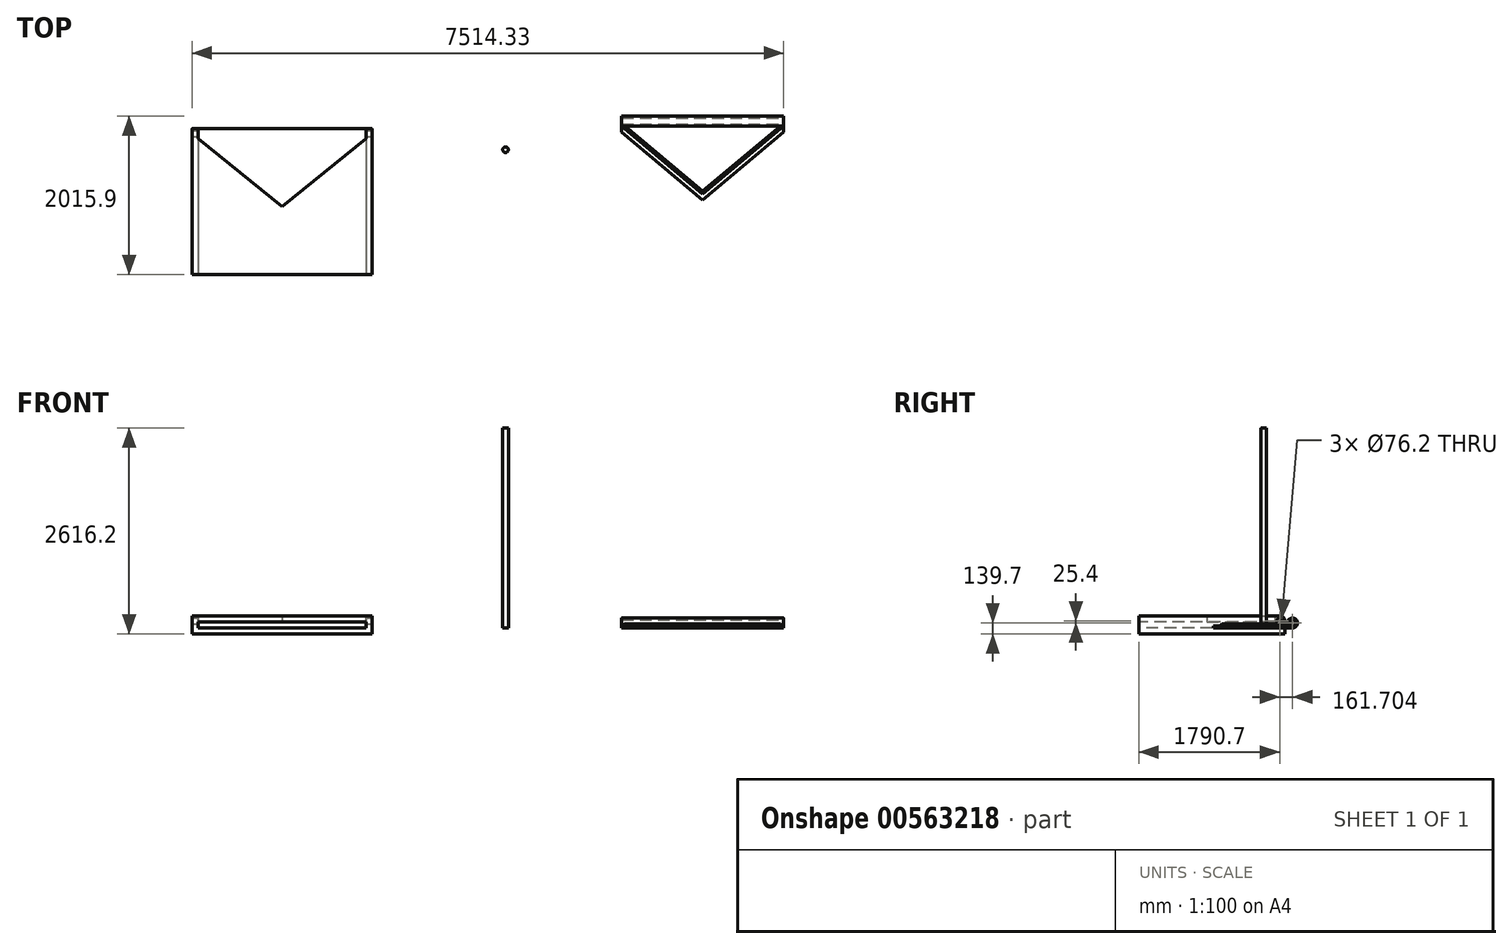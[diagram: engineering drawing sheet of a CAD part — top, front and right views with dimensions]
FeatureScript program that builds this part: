
annotation { "Feature Type Name" : "Feature", "Feature Type Description" : "" }
export const myFeature = defineFeature(function(context is Context, id is Id, definition is map)
    precondition{}
    {
        {
            var Q0;
            Q0=qCreatedBy(makeId("Top.planeOp"),FACE);
            var sketch = newSketch(context, id + "F0", { "sketchPlane" : qUnion([Q0])});
            skLineSegment(sketch, "E0.bottom", {"start": v(-1143, 863.6) * mm, "end": v(1143, 863.6) * mm});
            skLineSegment(sketch, "E0.top", {"start": v(-1143, -863.6) * mm, "end": v(1143, -863.6) * mm});
            skLineSegment(sketch, "E0.left", {"start": v(-1143, 863.6) * mm, "end": v(-1143, -863.6) * mm});
            skLineSegment(sketch, "E0.right", {"start": v(1143, 863.6) * mm, "end": v(1143, -863.6) * mm});
            skPoint(sketch, "E0.middle", {"position": v(0, 0) * mm});
            skSolve(sketch);
        }
        {
            var Q0;
            Q0 = qSketchRegion(id + "F0", true);
            extrude(context, id + "F1", {"entities" : qUnion([Q0]), "depth" : 76.2 * mm, "offsetDistance" : 25.4 * mm});
        }
        {
            var Q0;
            Q0=makeQuery(id+"F1.opExtrude","CAP_FACE",FACE,{"disambiguationData":[OSD([sQuery(id+"F0.wireOp",EDGE,"E0.bottom"),sQuery(id+"F0.wireOp",EDGE,"E0.top"),sQuery(id+"F0.wireOp",EDGE,"E0.left"),sQuery(id+"F0.wireOp",EDGE,"E0.right")])],"isStart":false});
            var sketch = newSketch(context, id + "F2", { "sketchPlane" : qUnion([Q0])});
            skLineSegment(sketch, "E1.bottom", {"start": v(-1143, 863.6) * mm, "end": v(-1066.8, 863.6) * mm});
            skLineSegment(sketch, "E1.top", {"start": v(-1143, -863.6) * mm, "end": v(-1066.8, -863.6) * mm});
            skLineSegment(sketch, "E1.left", {"start": v(-1143, 863.6) * mm, "end": v(-1143, -863.6) * mm});
            skLineSegment(sketch, "E1.right", {"start": v(-1066.8, 863.6) * mm, "end": v(-1066.8, -863.6) * mm});
            skLineSegment(sketch, "E2.bottom", {"start": v(1143, 863.6) * mm, "end": v(1066.8, 863.6) * mm});
            skLineSegment(sketch, "E2.top", {"start": v(1143, -863.6) * mm, "end": v(1066.8, -863.6) * mm});
            skLineSegment(sketch, "E2.left", {"start": v(1143, 863.6) * mm, "end": v(1143, -863.6) * mm});
            skLineSegment(sketch, "E2.right", {"start": v(1066.8, 863.6) * mm, "end": v(1066.8, -863.6) * mm});
            skSolve(sketch);
        }
        {
            var Q0;
            Q0 = qSketchRegion(id + "F2", true);
            extrude(context, id + "F3", {"entities" : qUnion([Q0]), "operationType" : NewBodyOperationType.ADD, "depth" : 76.2 * mm, "offsetDistance" : 25.4 * mm});
        }
        {
            var Q0;
            Q0=makeQuery(id+"F1.opExtrude","CAP_FACE",FACE,{"disambiguationData":[OSD([sQuery(id+"F0.wireOp",EDGE,"E0.bottom"),sQuery(id+"F0.wireOp",EDGE,"E0.top"),sQuery(id+"F0.wireOp",EDGE,"E0.left"),sQuery(id+"F0.wireOp",EDGE,"E0.right")])],"isStart":false});
            var sketch = newSketch(context, id + "F4", { "sketchPlane" : qUnion([Q0])});
            skLineSegment(sketch, "E3.bottom", {"start": v(-1143, -863.6) * mm, "end": v(1143, -863.6) * mm});
            skLineSegment(sketch, "E3.top", {"start": v(-1143, 863.6) * mm, "end": v(1143, 863.6) * mm});
            skLineSegment(sketch, "E3.left", {"start": v(-1143, -863.6) * mm, "end": v(-1143, 863.6) * mm});
            skLineSegment(sketch, "E3.right", {"start": v(1143, -863.6) * mm, "end": v(1143, 863.6) * mm});
            skPoint(sketch, "E3.middle", {"position": v(0, 0) * mm});
            skLineSegment(sketch, "E4", {"start": v(0, 0) * mm, "end": v(-1066.8, 863.6) * mm});
            skLineSegment(sketch, "E5", {"start": v(0, 0) * mm, "end": v(1066.8, 863.6) * mm});
            skSolve(sketch);
        }
        {
            var Q0;
            {var subQ2=sQuery(id+"F4.wireOp",EDGE,"E3.left");Q0=makeQuery(id+"F4.imprint","IMPRINT",FACE,{"disambiguationData":[TD([[makeQuery(id+"F4.imprint","IMPRINT",EDGE,{"derivedFrom":subQ2}),-1.0]])]});}
            var Q1;
            {var subQ2=sQuery(id+"F4.wireOp",EDGE,"E3.right");Q1=makeQuery(id+"F4.imprint","IMPRINT",FACE,{"disambiguationData":[TD([[makeQuery(id+"F4.imprint","IMPRINT",EDGE,{"derivedFrom":subQ2}),1.0]])]});}
            var Q2;
            Q2=makeQuery(id+"F4.imprint","IMPRINT",FACE,{"disambiguationData":[TD([[makeQuery(id+"F4.imprint","IMPRINT",EDGE,{"derivedFrom":sQuery(id+"F4.wireOp",EDGE,"E4")}),1.0]])]});
            extrude(context, id + "F5", {"entities" : qUnion([Q0, Q1, Q2]), "operationType" : NewBodyOperationType.ADD, "depth" : 152.4 * mm, "offsetDistance" : 25.4 * mm, "hasSecondDirection" : true, "secondDirectionOppositeDirection" : false, "secondDirectionDepth" : 76.2 * mm});
        }
        {
            var Q0;
            {var subQ0=sQuery(id+"F4.wireOp",EDGE,"E3.top");Q0=makeQuery(id+"F5.boolean.opBoolean","MERGE",FACE,{"derivedFrom":[makeQuery(id+"F3.boolean.opBoolean","MERGE",FACE,{"derivedFrom":[makeQuery(id+"F1.opExtrude","SWEPT_FACE",FACE,{"disambiguationData":[OSD([sQuery(id+"F0.wireOp",EDGE,"E0.bottom")])]}),makeQuery(id+"F3.opExtrude","SWEPT_FACE",FACE,{"disambiguationData":[OSD([sQuery(id+"F2.wireOp",EDGE,"E1.bottom")])]}),makeQuery(id+"F3.opExtrude","SWEPT_FACE",FACE,{"disambiguationData":[OSD([sQuery(id+"F2.wireOp",EDGE,"E2.bottom")])]})]}),makeQuery(id+"F5.opExtrude","SWEPT_FACE",FACE,{"disambiguationData":[OSD([subQ0]),TDD([makeQuery(id+"F4.imprint","IMPRINT",EDGE,{"disambiguationData":[TD([[makeQuery(id+"F4.imprint","INTERSECT",VERTEX,{"derivedFrom":[subQ0,sQuery(id+"F4.wireOp",EDGE,"E3.left")]}),-1.0]])],"derivedFrom":subQ0})])]}),makeQuery(id+"F5.opExtrude","SWEPT_FACE",FACE,{"disambiguationData":[OSD([subQ0]),TDD([makeQuery(id+"F4.imprint","IMPRINT",EDGE,{"disambiguationData":[TD([[makeQuery(id+"F4.imprint","INTERSECT",VERTEX,{"derivedFrom":[subQ0,sQuery(id+"F4.wireOp",EDGE,"E3.right")]}),1.0]])],"derivedFrom":subQ0})])]})]});}
            var sketch = newSketch(context, id + "F6", { "sketchPlane" : qUnion([Q0])});
            skLineSegment(sketch, "E6.bottom", {"start": v(-1143, 0) * mm, "end": v(-1066.8, 0) * mm});
            skLineSegment(sketch, "E6.top", {"start": v(-1143, 228.6) * mm, "end": v(-1066.8, 228.6) * mm});
            skLineSegment(sketch, "E6.left", {"start": v(-1143, 0) * mm, "end": v(-1143, 228.6) * mm});
            skLineSegment(sketch, "E6.right", {"start": v(-1066.8, 0) * mm, "end": v(-1066.8, 228.6) * mm});
            skLineSegment(sketch, "E7.bottom", {"start": v(1143, 0) * mm, "end": v(1066.8, 0) * mm});
            skLineSegment(sketch, "E7.top", {"start": v(1143, 228.6) * mm, "end": v(1066.8, 228.6) * mm});
            skLineSegment(sketch, "E7.left", {"start": v(1143, 0) * mm, "end": v(1143, 228.6) * mm});
            skLineSegment(sketch, "E7.right", {"start": v(1066.8, 0) * mm, "end": v(1066.8, 228.6) * mm});
            skSolve(sketch);
        }
        {
            var Q0;
            {var subQ3=sQuery(id+"F6.wireOp",EDGE,"E6.bottom");Q0=makeQuery(id+"F6.imprint","IMPRINT",FACE,{"disambiguationData":[TD([[makeQuery(id+"F6.imprint","IMPRINT",EDGE,{"derivedFrom":subQ3}),-1.0]])]});}
            var Q1;
            {var subQ3=sQuery(id+"F6.wireOp",EDGE,"E7.bottom");Q1=makeQuery(id+"F6.imprint","IMPRINT",FACE,{"disambiguationData":[TD([[makeQuery(id+"F6.imprint","IMPRINT",EDGE,{"derivedFrom":subQ3}),-1.0]])]});}
            var Q2;
            {var subQ1=sQuery(id+"F0.wireOp",EDGE,"E0.bottom");var subQ2=makeQuery(id+"F1.opExtrude","CAP_EDGE",EDGE,{"disambiguationData":[OSD([subQ1])],"isStart":false});Q2=makeQuery(id+"F6.imprint","IMPRINT",FACE,{"disambiguationData":[TD([[makeQuery(id+"F6.imprint","IMPRINT",EDGE,{"derivedFrom":subQ2}),1.0]])]});}
            extrude(context, id + "F7", {"entities" : qUnion([Q0, Q1, Q2]), "operationType" : NewBodyOperationType.ADD, "depth" : 127 * mm, "offsetDistance" : 25.4 * mm});
        }
        {
            var Q0;
            {var subQ0=sQuery(id+"F0.wireOp",EDGE,"E0.bottom");Q0=makeQuery(id+"F7.boolean.opBoolean","MERGE",FACE,{"derivedFrom":[makeQuery(id+"F1.opExtrude","CAP_FACE",FACE,{"disambiguationData":[OSD([subQ0,sQuery(id+"F0.wireOp",EDGE,"E0.top"),sQuery(id+"F0.wireOp",EDGE,"E0.left"),sQuery(id+"F0.wireOp",EDGE,"E0.right")])],"isStart":false}),makeQuery(id+"F7.opExtrude","SWEPT_FACE",FACE,{"disambiguationData":[OSD([subQ0])]})]});}
            var sketch = newSketch(context, id + "F8", { "sketchPlane" : qUnion([Q0])});
            skSolve(sketch);
        }
        {
            var Q0;
            Q0=makeQuery(id+"F7.boolean.opBoolean","MERGE",FACE,{"derivedFrom":[makeQuery(id+"F5.boolean.opBoolean","MERGE",FACE,{"derivedFrom":[makeQuery(id+"F3.boolean.opBoolean","MERGE",FACE,{"derivedFrom":[makeQuery(id+"F1.opExtrude","SWEPT_FACE",FACE,{"disambiguationData":[OSD([sQuery(id+"F0.wireOp",EDGE,"E0.right")])]}),makeQuery(id+"F3.opExtrude","SWEPT_FACE",FACE,{"disambiguationData":[OSD([sQuery(id+"F2.wireOp",EDGE,"E2.left")])]})]}),makeQuery(id+"F5.opExtrude","SWEPT_FACE",FACE,{"disambiguationData":[OSD([sQuery(id+"F4.wireOp",EDGE,"E3.right")])]})]}),makeQuery(id+"F7.opExtrude","SWEPT_FACE",FACE,{"disambiguationData":[OSD([sQuery(id+"F6.wireOp",EDGE,"E6.left")])]})]});
            var sketch = newSketch(context, id + "F9", { "sketchPlane" : qUnion([Q0])});
            skCircle(sketch, "E8", {"center": v(927.1, 165.1) * mm, "radius": 38.1 * mm});
            skSolve(sketch);
        }
        {
            var Q0;
            Q0=makeQuery(id+"F9.imprint","IMPRINT",FACE,{"disambiguationData":[TD([[makeQuery(id+"F9.imprint","IMPRINT",EDGE,{"derivedFrom":sQuery(id+"F9.wireOp",EDGE,"E8")}),1.0]])]});
            extrude(context, id + "F10", {"entities" : qUnion([Q0]), "operationType" : NewBodyOperationType.REMOVE, "oppositeDirection" : true, "depth" : 2291.08 * mm, "offsetDistance" : 25.4 * mm});
        }
        {
            var Q0;
            Q0=makeQuery(id+"F8.imprint","IMPRINT",FACE,{"disambiguationData":[TD([[makeQuery(id+"F8.imprint","IMPRINT",EDGE,{"derivedFrom":makeQuery(id+"F1.opExtrude","CAP_EDGE",EDGE,{"disambiguationData":[OSD([sQuery(id+"F0.wireOp",EDGE,"E0.top")])],"isStart":false})}),1.0]])]});
            var sketch = newSketch(context, id + "F11", { "sketchPlane" : qUnion([Q0])});
            skLineSegment(sketch, "E9.bottom", {"start": v(4313.93, 1025.3) * mm, "end": v(6371.33, 1025.3) * mm});
            skLineSegment(sketch, "E9.top", {"start": v(4313.93, 161.7) * mm, "end": v(6371.33, 161.7) * mm});
            skLineSegment(sketch, "E9.left", {"start": v(4313.93, 1025.3) * mm, "end": v(4313.93, 161.7) * mm});
            skLineSegment(sketch, "E9.right", {"start": v(6371.33, 1025.3) * mm, "end": v(6371.33, 161.7) * mm});
            skPoint(sketch, "E10", {"position": v(5342.63, 161.7) * mm});
            skLineSegment(sketch, "E11", {"start": v(4313.93, 1025.3) * mm, "end": v(5342.63, 161.7) * mm});
            skLineSegment(sketch, "E12", {"start": v(6371.33, 1025.3) * mm, "end": v(5342.63, 161.7) * mm});
            skLineSegment(sketch, "E13", {"start": v(5342.63, 161.7) * mm, "end": v(5342.63, 9.3) * mm});
            skPoint(sketch, "E14", {"position": v(4313.93, 949.1) * mm});
            skPoint(sketch, "E15", {"position": v(6371.33, 949.1) * mm});
            skPoint(sketch, "E16", {"position": v(5342.63, 85.5) * mm});
            skLineSegment(sketch, "E17", {"start": v(4313.93, 949.1) * mm, "end": v(5342.63, 85.5) * mm});
            skLineSegment(sketch, "E18", {"start": v(6371.33, 949.1) * mm, "end": v(5342.63, 85.5) * mm});
            skLineSegment(sketch, "E19.top", {"start": v(4313.93, 1152.3) * mm, "end": v(6371.33, 1152.3) * mm});
            skLineSegment(sketch, "E19.left", {"start": v(4313.93, 1025.3) * mm, "end": v(4313.93, 1152.3) * mm});
            skLineSegment(sketch, "E19.right", {"start": v(6371.33, 1025.3) * mm, "end": v(6371.33, 1152.3) * mm});
            skSolve(sketch);
        }
        {
            var Q0;
            Q0=makeQuery(id+"F11.imprint","IMPRINT",FACE,{"disambiguationData":[TD([[makeQuery(id+"F11.imprint","IMPRINT",EDGE,{"derivedFrom":sQuery(id+"F11.wireOp",EDGE,"E9.bottom")}),-1.0]])]});
            var Q1;
            Q1=makeQuery(id+"F11.imprint","IMPRINT",FACE,{"disambiguationData":[TD([[makeQuery(id+"F11.imprint","IMPRINT",EDGE,{"derivedFrom":sQuery(id+"F11.wireOp",EDGE,"E11")}),1.0]])]});
            extrude(context, id + "F12", {"entities" : qUnion([Q0, Q1]), "depth" : 50.8 * mm, "offsetDistance" : 25.4 * mm});
        }
        {
            var Q0;
            {var subQ0=sQuery(id+"F11.wireOp",EDGE,"E11");Q0=makeQuery(id+"F11.imprint","IMPRINT",FACE,{"disambiguationData":[TD([[makeQuery(id+"F11.imprint","IMPRINT",EDGE,{"derivedFrom":subQ0}),-1.0]])]});}
            var Q1;
            {var subQ0=sQuery(id+"F11.wireOp",EDGE,"E12");Q1=makeQuery(id+"F11.imprint","IMPRINT",FACE,{"disambiguationData":[TD([[makeQuery(id+"F11.imprint","IMPRINT",EDGE,{"derivedFrom":subQ0}),1.0]])]});}
            var Q2;
            {var subQ1=sQuery(id+"F11.wireOp",EDGE,"E9.top");var subQ3=sQuery(id+"F11.wireOp",EDGE,"E18");var subQ4=makeQuery(id+"F11.imprint","INTERSECT",VERTEX,{"derivedFrom":[subQ1,subQ3]});Q2=makeQuery(id+"F11.imprint","IMPRINT",FACE,{"disambiguationData":[TD([[makeQuery(id+"F11.imprint","IMPRINT",EDGE,{"disambiguationData":[TD([[subQ4,-1.0]])],"derivedFrom":subQ3}),-1.0]])]});}
            var Q3;
            {var subQ1=sQuery(id+"F11.wireOp",EDGE,"E9.top");var subQ3=sQuery(id+"F11.wireOp",EDGE,"E17");var subQ4=makeQuery(id+"F11.imprint","INTERSECT",VERTEX,{"derivedFrom":[subQ1,subQ3]});Q3=makeQuery(id+"F11.imprint","IMPRINT",FACE,{"disambiguationData":[TD([[makeQuery(id+"F11.imprint","IMPRINT",EDGE,{"disambiguationData":[TD([[subQ4,-1.0]])],"derivedFrom":subQ3}),1.0]])]});}
            extrude(context, id + "F13", {"entities" : qUnion([Q0, Q1, Q2, Q3]), "operationType" : NewBodyOperationType.ADD, "depth" : 25.4 * mm, "offsetDistance" : 25.4 * mm});
        }
        {
            var Q0;
            Q0=makeQuery(id+"F11.imprint","IMPRINT",FACE,{"disambiguationData":[TD([[makeQuery(id+"F11.imprint","IMPRINT",EDGE,{"derivedFrom":sQuery(id+"F11.wireOp",EDGE,"E9.bottom")}),1.0]])]});
            extrude(context, id + "F14", {"entities" : qUnion([Q0]), "operationType" : NewBodyOperationType.ADD, "depth" : 127 * mm, "offsetDistance" : 25.4 * mm});
        }
        {
            var Q0;
            Q0=makeQuery(id+"F14.boolean.opBoolean","MERGE",FACE,{"derivedFrom":[makeQuery(id+"F13.opExtrude","SWEPT_FACE",FACE,{"disambiguationData":[OSD([sQuery(id+"F11.wireOp",EDGE,"E9.right")])]}),makeQuery(id+"F14.opExtrude","SWEPT_FACE",FACE,{"disambiguationData":[OSD([sQuery(id+"F11.wireOp",EDGE,"E19.right")])]})]});
            var sketch = newSketch(context, id + "F15", { "sketchPlane" : qUnion([Q0])});
            skCircle(sketch, "E20", {"center": v(1088.8, 139.7) * mm, "radius": 38.1 * mm});
            skSolve(sketch);
        }
        {
            var Q0;
            Q0=makeQuery(id+"F15.imprint","IMPRINT",FACE,{"disambiguationData":[TD([[makeQuery(id+"F15.imprint","IMPRINT",EDGE,{"derivedFrom":sQuery(id+"F15.wireOp",EDGE,"E20")}),1.0]])]});
            extrude(context, id + "F16", {"entities" : qUnion([Q0]), "operationType" : NewBodyOperationType.REMOVE, "oppositeDirection" : true, "depth" : 2276.86 * mm, "offsetDistance" : 25.4 * mm});
        }
        {
            var Q0;
            Q0=makeQuery(id+"F14.opExtrude","CAP_EDGE",EDGE,{"disambiguationData":[OSD([sQuery(id+"F11.wireOp",EDGE,"E19.top")])],"isStart":false});
            var Q1;
            Q1=makeQuery(id+"F14.opExtrude","CAP_EDGE",EDGE,{"disambiguationData":[OSD([sQuery(id+"F11.wireOp",EDGE,"E9.bottom")])],"isStart":false});
            var Q2;
            Q2=makeQuery(id+"F14.opExtrude","CAP_EDGE",EDGE,{"disambiguationData":[OSD([sQuery(id+"F11.wireOp",EDGE,"E19.top")])],"isStart":true});
            fillet(context, id + "F17", {"entities" : qUnion([Q0, Q1, Q2]), "radius" : 63.5 * mm, "tangentPropagation" : true, "allowEdgeOverflow" : false});
        }
        {
            var Q0;
            Q0=makeQuery(id+"F12.opExtrude","CAP_EDGE",EDGE,{"disambiguationData":[OSD([sQuery(id+"F11.wireOp",EDGE,"E11")])],"isStart":false});
            chamfer(context, id + "F18", {"entities" : qUnion([Q0]), "width" : 25.4 * mm, "tangentPropagation" : true});
        }
        {
            var Q0;
            Q0=makeQuery(id+"F12.opExtrude","CAP_EDGE",EDGE,{"disambiguationData":[OSD([sQuery(id+"F11.wireOp",EDGE,"E12")])],"isStart":false});
            chamfer(context, id + "F19", {"entities" : qUnion([Q0]), "width" : 25.4 * mm, "tangentPropagation" : true});
        }
        {
            var Q0;
            Q0=makeQuery(id+"F7.opExtrude","CAP_EDGE",EDGE,{"disambiguationData":[OSD([sQuery(id+"F6.wireOp",EDGE,"E7.top")])],"isStart":false});
            var Q1;
            Q1=makeQuery(id+"F7.opExtrude","CAP_EDGE",EDGE,{"disambiguationData":[OSD([sQuery(id+"F6.wireOp",EDGE,"E6.top")])],"isStart":false});
            fillet(context, id + "F20", {"entities" : qUnion([Q0, Q1]), "radius" : 63.5 * mm, "tangentPropagation" : true, "allowEdgeOverflow" : false});
        }
        {
            var Q0;
            Q0=makeQuery(id+"F11.imprint","IMPRINT",FACE,{"disambiguationData":[TD([[makeQuery(id+"F11.imprint","IMPRINT",EDGE,{"derivedFrom":makeQuery(id+"F8.imprint","IMPRINT",EDGE,{"derivedFrom":makeQuery(id+"F1.opExtrude","CAP_EDGE",EDGE,{"disambiguationData":[OSD([sQuery(id+"F0.wireOp",EDGE,"E0.top")])],"isStart":false})})}),1.0]])]});
            var sketch = newSketch(context, id + "F21", { "sketchPlane" : qUnion([Q0])});
            skCircle(sketch, "E21", {"center": v(2838.58, 722.66) * mm, "radius": 35.56 * mm});
            skSolve(sketch);
        }
        {
            var Q0;
            Q0=makeQuery(id+"F21.imprint","IMPRINT",FACE,{"disambiguationData":[TD([[makeQuery(id+"F21.imprint","IMPRINT",EDGE,{"derivedFrom":sQuery(id+"F21.wireOp",EDGE,"E21")}),1.0]])]});
            extrude(context, id + "F22", {"entities" : qUnion([Q0]), "depth" : 2540 * mm, "offsetDistance" : 25.4 * mm});
        }
    });
